# Revit family: Mirror_Metlam_Framed
name_source: partatom
category: Specialty Equipment
revit_build: Autodesk Revit 2016 (Build: 20161004_0715(x64)
units: mm (PartAtom-declared; Revit-internal decimal feet)

## family parameters
Always vertical = Yes
Cut with Voids When Loaded = No
OmniClass Number = 23.40.95.17.17
OmniClass Title = Mirrors
Part Type = Normal
Room Calculation Point = Yes
Round Connector Dimension = Use Diameter
Shared = No
Work Plane-Based = No

## types (7) — shared parameters
Description = Stainless Steel Framed Mirror
Manufacturer = Metlam
Manufacturer_Overall Depth = 25 mm  [stored 0.082021 ft]
Manufacturer_URL__Product Specific = https://metlam.com.au
Material_ANZRS = z_Metlam_Metal_Stainless Steel_Satin
Mirror_Material = z_Metlam_Glass_Mirror
Type Comments = Mirrors
URL = http://www.metlam.com.au

## per-type parameters (varying)
| type | Manufacturer_Overall Height | Manufacturer_Overall Width | Manufacturer_Spec Code | Model |
| 460w x 25d x 610h (ML771) | 610 mm  [stored 2.00131 ft] | 460 mm  [stored 1.50919 ft] | ML771 | ML771 |
| 460w x 25d x 760h (ML771_1) | 760 mm | 460 mm  [stored 1.50919 ft] | ML771_1 | ML771_1 |
| 460w x 25d x 910h (ML771_2) | 910 mm | 460 mm  [stored 1.50919 ft] | ML771_2 | ML771_2 |
| 610w x 25d x 760h (ML771_3) | 760 mm | 610 mm  [stored 2.00131 ft] | ML771_3 | ML771_3 |
| 610w x 25d x 910h (ML771_4) | 910 mm | 610 mm  [stored 2.00131 ft] | ML771_4 | ML771_4 |
| 450w x 25d x 1000h (ML771_5) | 1000 mm  [stored 3.28084 ft] | 450 mm  [stored 1.47638 ft] | ML771_5 | ML771_5 |
| 600w x 25d x 1000h (ML771_6) | 1000 mm  [stored 3.28084 ft] | 600 mm | ML771_6 | ML771_6 |

note: [stored X ft] marks values corroborated as IEEE doubles in the binary element streams (Revit-internal decimal feet)

## geometry (parser evidence)
native form markers: Sweep x3
no freeform markers — native parametric forms only
